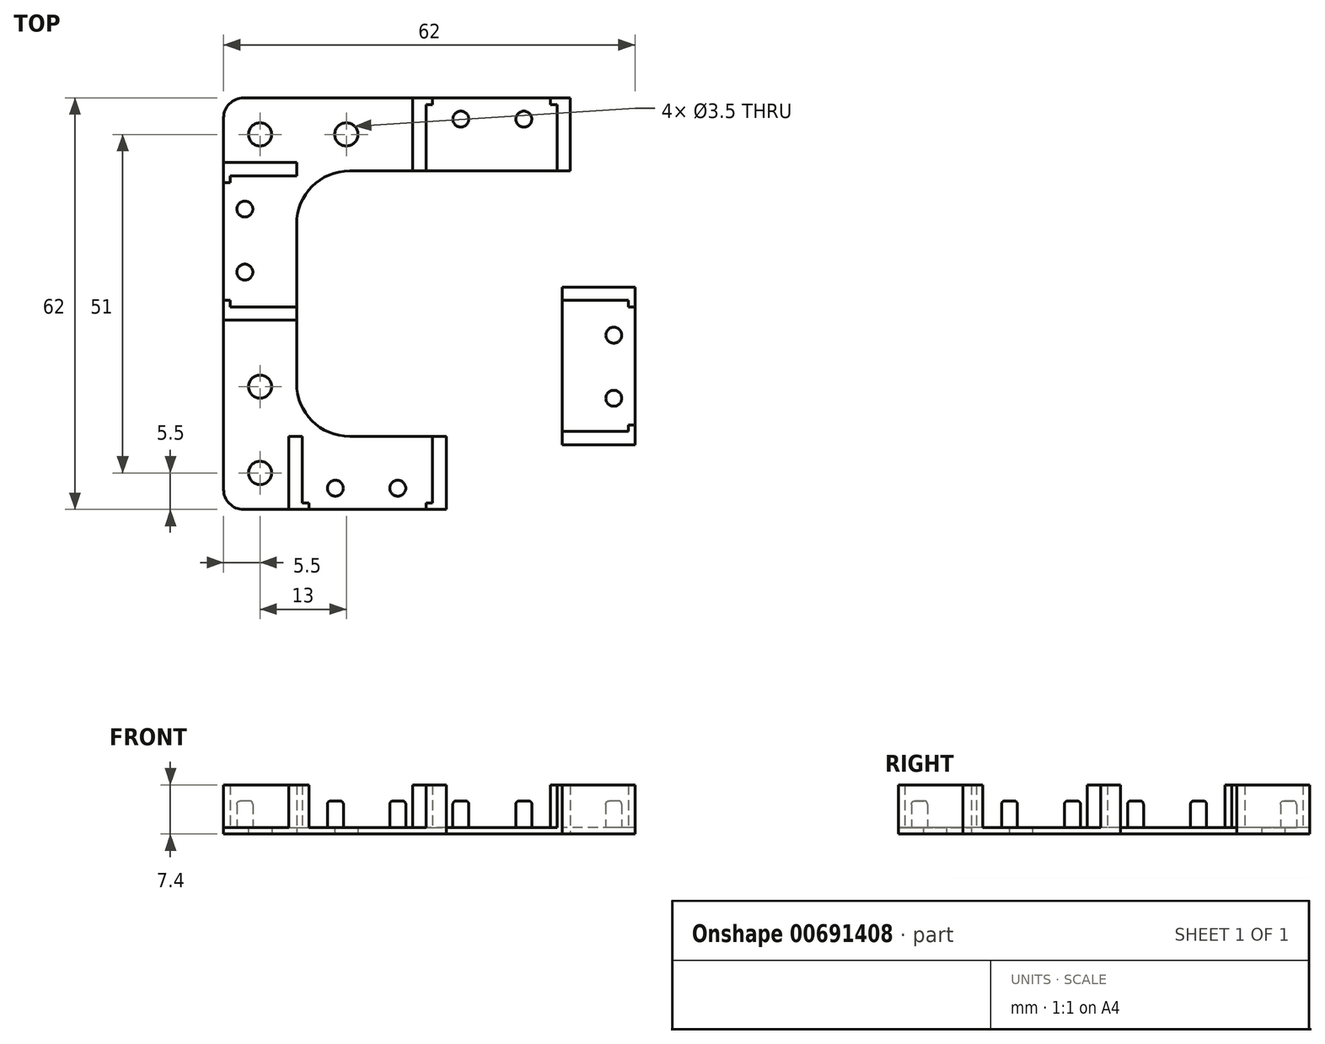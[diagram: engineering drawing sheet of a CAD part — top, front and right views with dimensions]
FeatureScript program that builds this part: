
annotation { "Feature Type Name" : "Feature", "Feature Type Description" : "" }
export const myFeature = defineFeature(function(context is Context, id is Id, definition is map)
    precondition{}
    {
        {
            var Q0;
            Q0=qCreatedBy(makeId("Top.planeOp"),FACE);
            var sketch = newSketch(context, id + "F0", { "sketchPlane" : qUnion([Q0])});
            skLineSegment(sketch, "E0.bottom", {"start": v(0, 20) * mm, "end": v(20, 20) * mm});
            skLineSegment(sketch, "E0.top", {"start": v(0, -20) * mm, "end": v(20, -20) * mm});
            skLineSegment(sketch, "E0.right", {"start": v(20, 20) * mm, "end": v(20, -20) * mm});
            skPoint(sketch, "E1", {"position": v(0, 20) * mm});
            skPoint(sketch, "E2", {"position": v(0, -20) * mm});
            skPoint(sketch, "E3", {"position": v(20, 0) * mm});
            skLineSegment(sketch, "E4.bottom", {"start": v(0, 31) * mm, "end": v(31, 31) * mm});
            skLineSegment(sketch, "E4.top", {"start": v(0, -31) * mm, "end": v(31, -31) * mm});
            skLineSegment(sketch, "E4.right", {"start": v(31, 31) * mm, "end": v(31, -31) * mm});
            skPoint(sketch, "E5", {"position": v(0, 31) * mm});
            skPoint(sketch, "E6", {"position": v(31, 0) * mm});
            skLineSegment(sketch, "E7.bottom", {"start": v(20, 2.5) * mm, "end": v(31, 2.5) * mm});
            skLineSegment(sketch, "E7.top", {"start": v(20, -21.25) * mm, "end": v(31, -21.25) * mm});
            skLineSegment(sketch, "E7.left", {"start": v(20, 2.5) * mm, "end": v(20, -21.25) * mm});
            skLineSegment(sketch, "E7.right", {"start": v(31, 2.5) * mm, "end": v(31, -21.25) * mm});
            skLineSegment(sketch, "E8", {"start": v(31, -0.5) * mm, "end": v(30, -0.5) * mm});
            skLineSegment(sketch, "E9", {"start": v(30, -0.5) * mm, "end": v(30, 0.5) * mm});
            skLineSegment(sketch, "E10", {"start": v(30, 0.5) * mm, "end": v(20, 0.5) * mm});
            skLineSegment(sketch, "E11", {"start": v(31, -18.25) * mm, "end": v(30, -18.25) * mm});
            skLineSegment(sketch, "E12", {"start": v(30, -18.25) * mm, "end": v(30, -19.25) * mm});
            skLineSegment(sketch, "E13", {"start": v(30, -19.25) * mm, "end": v(20, -19.25) * mm});
            skCircle(sketch, "E14", {"center": v(27.8, -14.25) * mm, "radius": 1.2 * mm});
            skCircle(sketch, "E15", {"center": v(27.8, -4.75) * mm, "radius": 1.2 * mm});
            skLineSegment(sketch, "E16", {"start": v(27.8, -4.75) * mm, "end": v(27.8, 0.5) * mm, "construction": true});
            skPoint(sketch, "E17", {"position": v(0, -31) * mm});
            skLineSegment(sketch, "E18.bottom", {"start": v(-17.16, -20) * mm, "end": v(2.6, -20) * mm});
            skLineSegment(sketch, "E18.top", {"start": v(-17.16, -31) * mm, "end": v(-3.68, -31) * mm});
            skLineSegment(sketch, "E18.left", {"start": v(-21.15, -20) * mm, "end": v(-21.15, -31) * mm});
            skLineSegment(sketch, "E18.right", {"start": v(2.6, -20) * mm, "end": v(2.6, -31) * mm});
            skLineSegment(sketch, "E19", {"start": v(-18.15, -31) * mm, "end": v(-18.15, -30) * mm});
            skLineSegment(sketch, "E20", {"start": v(-19.15, -30) * mm, "end": v(-19.15, -20) * mm});
            skLineSegment(sketch, "E21", {"start": v(-0.5, -31) * mm, "end": v(-0.5, -30) * mm});
            skLineSegment(sketch, "E22", {"start": v(-0.5, -30) * mm, "end": v(0.5, -30) * mm});
            skLineSegment(sketch, "E23", {"start": v(0.5, -30) * mm, "end": v(0.5, -20) * mm});
            skCircle(sketch, "E24", {"center": v(-14.15, -27.8) * mm, "radius": 1.2 * mm});
            skCircle(sketch, "E25", {"center": v(-4.75, -27.8) * mm, "radius": 1.2 * mm});
            skLineSegment(sketch, "E26.MirrorCS", {"start": v(0, 31) * mm, "end": v(-31, 31) * mm});
            skLineSegment(sketch, "E27.MirrorCS", {"start": v(0, 20) * mm, "end": v(-20, 20) * mm});
            skLineSegment(sketch, "E28.MirrorCS", {"start": v(-31, 31) * mm, "end": v(-31, -31) * mm});
            skLineSegment(sketch, "E29.MirrorCS", {"start": v(0, -31) * mm, "end": v(-31, -31) * mm});
            skLineSegment(sketch, "E30", {"start": v(-20, 20) * mm, "end": v(-20, -20) * mm});
            skLineSegment(sketch, "E31", {"start": v(-20, -20) * mm, "end": v(0, -20) * mm});
            skLineSegment(sketch, "E32.bottom", {"start": v(-31, 21.25) * mm, "end": v(-20, 21.25) * mm});
            skLineSegment(sketch, "E32.top", {"start": v(-31, -2.5) * mm, "end": v(-20, -2.5) * mm});
            skLineSegment(sketch, "E32.left", {"start": v(-31, 21.25) * mm, "end": v(-31, -2.5) * mm});
            skLineSegment(sketch, "E32.right", {"start": v(-20, 21.25) * mm, "end": v(-20, -2.5) * mm});
            skLineSegment(sketch, "E33", {"start": v(-31, 18.25) * mm, "end": v(-30, 18.25) * mm});
            skLineSegment(sketch, "E34", {"start": v(-30, 18.25) * mm, "end": v(-30, 19.25) * mm});
            skLineSegment(sketch, "E35", {"start": v(-30, 19.25) * mm, "end": v(-20, 19.25) * mm});
            skLineSegment(sketch, "E36", {"start": v(-31, 0.5) * mm, "end": v(-30, 0.5) * mm});
            skLineSegment(sketch, "E37", {"start": v(-30, 0.5) * mm, "end": v(-30, -0.5) * mm});
            skLineSegment(sketch, "E38", {"start": v(-30, -0.5) * mm, "end": v(-20, -0.5) * mm});
            skCircle(sketch, "E39", {"center": v(-27.8, 14.25) * mm, "radius": 1.2 * mm});
            skCircle(sketch, "E40", {"center": v(-27.8, 4.75) * mm, "radius": 1.2 * mm});
            skPoint(sketch, "E41.startSnap0", {"position": v(-31, 0) * mm});
            skLineSegment(sketch, "E42", {"start": v(-19.15, -30) * mm, "end": v(-18.15, -30) * mm});
            skLineSegment(sketch, "E43", {"start": v(-21.15, -20) * mm, "end": v(-20, -20) * mm});
            skLineSegment(sketch, "E44.bottom", {"start": v(-2.5, 31) * mm, "end": v(21.25, 31) * mm});
            skLineSegment(sketch, "E44.top", {"start": v(-2.5, 20) * mm, "end": v(21.25, 20) * mm});
            skLineSegment(sketch, "E44.left", {"start": v(-2.5, 31) * mm, "end": v(-2.5, 20) * mm});
            skLineSegment(sketch, "E44.right", {"start": v(21.25, 31) * mm, "end": v(21.25, 20) * mm});
            skLineSegment(sketch, "E45", {"start": v(0.5, 31) * mm, "end": v(0.5, 30) * mm});
            skLineSegment(sketch, "E46", {"start": v(0.5, 30) * mm, "end": v(-0.5, 30) * mm});
            skLineSegment(sketch, "E47", {"start": v(-0.5, 30) * mm, "end": v(-0.5, 20) * mm});
            skLineSegment(sketch, "E48", {"start": v(18.25, 31) * mm, "end": v(18.25, 30) * mm});
            skLineSegment(sketch, "E49", {"start": v(18.25, 30) * mm, "end": v(19.25, 30) * mm});
            skLineSegment(sketch, "E50", {"start": v(19.25, 30) * mm, "end": v(19.25, 20) * mm});
            skCircle(sketch, "E51", {"center": v(4.75, 27.8) * mm, "radius": 1.2 * mm});
            skCircle(sketch, "E52", {"center": v(14.25, 27.8) * mm, "radius": 1.2 * mm});
            skCircle(sketch, "E53", {"center": v(25.5, 25.5) * mm, "radius": 1.75 * mm});
            skCircle(sketch, "E54", {"center": v(-25.5, 25.5) * mm, "radius": 1.75 * mm});
            skCircle(sketch, "E55", {"center": v(-25.5, -25.5) * mm, "radius": 1.75 * mm});
            skCircle(sketch, "E56", {"center": v(25.5, -25.5) * mm, "radius": 1.75 * mm});
            skCircle(sketch, "E57", {"center": v(12.6, -25.5) * mm, "radius": 1.75 * mm});
            skPoint(sketch, "E57.centerSnap0", {"position": v(2.6, -25.5) * mm});
            skCircle(sketch, "E58", {"center": v(-25.5, -12.5) * mm, "radius": 1.75 * mm});
            skCircle(sketch, "E59", {"center": v(-12.5, 25.5) * mm, "radius": 1.75 * mm});
            skCircle(sketch, "E60", {"center": v(25.5, 12.5) * mm, "radius": 1.75 * mm});
            skSolve(sketch);
        }
        {
            var Q0;
            {var subQ1=sQuery(id+"F0.wireOp",EDGE,"E44.left");Q0=makeQuery(id+"F0.imprint","IMPRINT",FACE,{"disambiguationData":[TD([[makeQuery(id+"F0.imprint","IMPRINT",EDGE,{"derivedFrom":subQ1}),1.0]])]});}
            var Q1;
            {var subQ0=sQuery(id+"F0.wireOp",EDGE,"E44.right");Q1=makeQuery(id+"F0.imprint","IMPRINT",FACE,{"disambiguationData":[TD([[makeQuery(id+"F0.imprint","IMPRINT",EDGE,{"derivedFrom":subQ0}),-1.0]])]});}
            var Q2;
            {var subQ2=sQuery(id+"F0.wireOp",EDGE,"E7.bottom");Q2=makeQuery(id+"F0.imprint","IMPRINT",FACE,{"disambiguationData":[TD([[makeQuery(id+"F0.imprint","IMPRINT",EDGE,{"derivedFrom":subQ2}),-1.0]])]});}
            var Q3;
            {var subQ1=sQuery(id+"F0.wireOp",EDGE,"E7.top");Q3=makeQuery(id+"F0.imprint","IMPRINT",FACE,{"disambiguationData":[TD([[makeQuery(id+"F0.imprint","IMPRINT",EDGE,{"derivedFrom":subQ1}),1.0]])]});}
            var Q4;
            {var subQ0=sQuery(id+"F0.wireOp",EDGE,"E18.right");Q4=makeQuery(id+"F0.imprint","IMPRINT",FACE,{"disambiguationData":[TD([[makeQuery(id+"F0.imprint","IMPRINT",EDGE,{"derivedFrom":subQ0}),-1.0]])]});}
            var Q5;
            {var subQ3=sQuery(id+"F0.wireOp",EDGE,"E18.left");Q5=makeQuery(id+"F0.imprint","IMPRINT",FACE,{"disambiguationData":[TD([[makeQuery(id+"F0.imprint","IMPRINT",EDGE,{"derivedFrom":subQ3}),1.0]])]});}
            var Q6;
            {var subQ1=sQuery(id+"F0.wireOp",EDGE,"E32.top");Q6=makeQuery(id+"F0.imprint","IMPRINT",FACE,{"disambiguationData":[TD([[makeQuery(id+"F0.imprint","IMPRINT",EDGE,{"derivedFrom":subQ1}),1.0]])]});}
            var Q7;
            {var subQ4=sQuery(id+"F0.wireOp",EDGE,"E32.bottom");Q7=makeQuery(id+"F0.imprint","IMPRINT",FACE,{"disambiguationData":[TD([[makeQuery(id+"F0.imprint","IMPRINT",EDGE,{"derivedFrom":subQ4}),-1.0]])]});}
            extrude(context, id + "F1", {"entities" : qUnion([Q0, Q1, Q2, Q3, Q4, Q5, Q6, Q7]), "depth" : 7.4 * mm, "offsetDistance" : 25 * mm});
        }
        {
            var Q0;
            Q0=makeQuery(id+"F0.imprint","IMPRINT",FACE,{"disambiguationData":[TD([[makeQuery(id+"F0.imprint","IMPRINT",EDGE,{"derivedFrom":sQuery(id+"F0.wireOp",EDGE,"E51")}),1.0]])]});
            var Q1;
            Q1=makeQuery(id+"F0.imprint","IMPRINT",FACE,{"disambiguationData":[TD([[makeQuery(id+"F0.imprint","IMPRINT",EDGE,{"derivedFrom":sQuery(id+"F0.wireOp",EDGE,"E52")}),1.0]])]});
            var Q2;
            Q2=makeQuery(id+"F0.imprint","IMPRINT",FACE,{"disambiguationData":[TD([[makeQuery(id+"F0.imprint","IMPRINT",EDGE,{"derivedFrom":sQuery(id+"F0.wireOp",EDGE,"E15")}),1.0]])]});
            var Q3;
            Q3=makeQuery(id+"F0.imprint","IMPRINT",FACE,{"disambiguationData":[TD([[makeQuery(id+"F0.imprint","IMPRINT",EDGE,{"derivedFrom":sQuery(id+"F0.wireOp",EDGE,"E14")}),1.0]])]});
            var Q4;
            Q4=makeQuery(id+"F0.imprint","IMPRINT",FACE,{"disambiguationData":[TD([[makeQuery(id+"F0.imprint","IMPRINT",EDGE,{"derivedFrom":sQuery(id+"F0.wireOp",EDGE,"E25")}),1.0]])]});
            var Q5;
            Q5=makeQuery(id+"F0.imprint","IMPRINT",FACE,{"disambiguationData":[TD([[makeQuery(id+"F0.imprint","IMPRINT",EDGE,{"derivedFrom":sQuery(id+"F0.wireOp",EDGE,"E24")}),1.0]])]});
            var Q6;
            Q6=makeQuery(id+"F0.imprint","IMPRINT",FACE,{"disambiguationData":[TD([[makeQuery(id+"F0.imprint","IMPRINT",EDGE,{"derivedFrom":sQuery(id+"F0.wireOp",EDGE,"E39")}),1.0]])]});
            var Q7;
            Q7=makeQuery(id+"F0.imprint","IMPRINT",FACE,{"disambiguationData":[TD([[makeQuery(id+"F0.imprint","IMPRINT",EDGE,{"derivedFrom":sQuery(id+"F0.wireOp",EDGE,"E40")}),1.0]])]});
            extrude(context, id + "F2", {"entities" : qUnion([Q0, Q1, Q2, Q3, Q4, Q5, Q6, Q7]), "operationType" : NewBodyOperationType.ADD, "depth" : 5 * mm, "offsetDistance" : 25 * mm});
        }
        {
            var Q0;
            {var subQ0=sQuery(id+"F0.wireOp",EDGE,"E45");Q0=makeQuery(id+"F0.imprint","IMPRINT",FACE,{"disambiguationData":[TD([[makeQuery(id+"F0.imprint","IMPRINT",EDGE,{"derivedFrom":subQ0}),1.0]])]});}
            var Q1;
            {var subQ3=sQuery(id+"F0.wireOp",EDGE,"E26.MirrorCS");Q1=makeQuery(id+"F0.imprint","IMPRINT",FACE,{"disambiguationData":[TD([[makeQuery(id+"F0.imprint","IMPRINT",EDGE,{"derivedFrom":subQ3}),1.0]])]});}
            var Q2;
            {var subQ0=sQuery(id+"F0.wireOp",EDGE,"E33");Q2=makeQuery(id+"F0.imprint","IMPRINT",FACE,{"disambiguationData":[TD([[makeQuery(id+"F0.imprint","IMPRINT",EDGE,{"derivedFrom":subQ0}),-1.0]])]});}
            var Q3;
            {var subQ1=sQuery(id+"F0.wireOp",EDGE,"E18.left");Q3=makeQuery(id+"F0.imprint","IMPRINT",FACE,{"disambiguationData":[TD([[makeQuery(id+"F0.imprint","IMPRINT",EDGE,{"derivedFrom":subQ1}),-1.0]])]});}
            var Q4;
            {var subQ7=sQuery(id+"F0.wireOp",EDGE,"E19");Q4=makeQuery(id+"F0.imprint","IMPRINT",FACE,{"disambiguationData":[TD([[makeQuery(id+"F0.imprint","IMPRINT",EDGE,{"derivedFrom":subQ7}),-1.0]])]});}
            var Q5;
            {var subQ5=sQuery(id+"F0.wireOp",EDGE,"E0.top");Q5=makeQuery(id+"F0.imprint","IMPRINT",FACE,{"disambiguationData":[TD([[makeQuery(id+"F0.imprint","IMPRINT",EDGE,{"derivedFrom":subQ5}),-1.0]])]});}
            var Q6;
            {var subQ0=sQuery(id+"F0.wireOp",EDGE,"E8");Q6=makeQuery(id+"F0.imprint","IMPRINT",FACE,{"disambiguationData":[TD([[makeQuery(id+"F0.imprint","IMPRINT",EDGE,{"derivedFrom":subQ0}),1.0]])]});}
            var Q7;
            {var subQ3=sQuery(id+"F0.wireOp",EDGE,"E0.right");Q7=makeQuery(id+"F0.imprint","IMPRINT",FACE,{"disambiguationData":[TD([[makeQuery(id+"F0.imprint","IMPRINT",EDGE,{"derivedFrom":subQ3}),1.0]])]});}
            extrude(context, id + "F3", {"entities" : qUnion([Q0, Q1, Q2, Q3, Q4, Q5, Q6, Q7]), "operationType" : NewBodyOperationType.ADD, "depth" : 1 * mm, "offsetDistance" : 25 * mm});
        }
        {
            var Q0;
            Q0=makeQuery(id+"F3.opExtrude","SWEPT_EDGE",EDGE,{"disambiguationData":[OSD([sQuery(id+"F0.wireOp",EDGE,"E26.MirrorCS"),sQuery(id+"F0.wireOp",EDGE,"E28.MirrorCS")])]});
            var Q1;
            Q1=makeQuery(id+"F3.opExtrude","SWEPT_EDGE",EDGE,{"disambiguationData":[OSD([sQuery(id+"F0.wireOp",EDGE,"E4.bottom"),sQuery(id+"F0.wireOp",EDGE,"E4.right")])]});
            var Q2;
            Q2=makeQuery(id+"F3.opExtrude","SWEPT_EDGE",EDGE,{"disambiguationData":[OSD([sQuery(id+"F0.wireOp",EDGE,"E4.top"),sQuery(id+"F0.wireOp",EDGE,"E4.right")])]});
            var Q3;
            Q3=makeQuery(id+"F3.opExtrude","SWEPT_EDGE",EDGE,{"disambiguationData":[OSD([sQuery(id+"F0.wireOp",EDGE,"E28.MirrorCS"),sQuery(id+"F0.wireOp",EDGE,"E29.MirrorCS")])]});
            fillet(context, id + "F4", {"entities" : qUnion([Q0, Q1, Q2, Q3]), "radius" : 3 * mm, "tangentPropagation" : true, "allowEdgeOverflow" : false});
        }
        {
            var Q0;
            Q0=makeQuery(id+"F2.opExtrude","CAP_EDGE",EDGE,{"disambiguationData":[OSD([sQuery(id+"F0.wireOp",EDGE,"E52")])],"isStart":false});
            var Q1;
            Q1=makeQuery(id+"F2.opExtrude","CAP_EDGE",EDGE,{"disambiguationData":[OSD([sQuery(id+"F0.wireOp",EDGE,"E51")])],"isStart":false});
            var Q2;
            Q2=makeQuery(id+"F2.opExtrude","CAP_EDGE",EDGE,{"disambiguationData":[OSD([sQuery(id+"F0.wireOp",EDGE,"E39")])],"isStart":false});
            var Q3;
            Q3=makeQuery(id+"F2.opExtrude","CAP_EDGE",EDGE,{"disambiguationData":[OSD([sQuery(id+"F0.wireOp",EDGE,"E40")])],"isStart":false});
            var Q4;
            Q4=makeQuery(id+"F2.opExtrude","CAP_EDGE",EDGE,{"disambiguationData":[OSD([sQuery(id+"F0.wireOp",EDGE,"E15")])],"isStart":false});
            var Q5;
            Q5=makeQuery(id+"F2.opExtrude","CAP_EDGE",EDGE,{"disambiguationData":[OSD([sQuery(id+"F0.wireOp",EDGE,"E14")])],"isStart":false});
            var Q6;
            Q6=makeQuery(id+"F2.opExtrude","CAP_EDGE",EDGE,{"disambiguationData":[OSD([sQuery(id+"F0.wireOp",EDGE,"E25")])],"isStart":false});
            var Q7;
            Q7=makeQuery(id+"F2.opExtrude","CAP_EDGE",EDGE,{"disambiguationData":[OSD([sQuery(id+"F0.wireOp",EDGE,"E24")])],"isStart":false});
            fillet(context, id + "F5", {"entities" : qUnion([Q0, Q1, Q2, Q3, Q4, Q5, Q6, Q7]), "radius" : 0.5 * mm, "tangentPropagation" : true, "allowEdgeOverflow" : false});
        }
        {
            var Q0;
            Q0=makeQuery(id+"F3.opExtrude","SWEPT_EDGE",EDGE,{"disambiguationData":[OSD([sQuery(id+"F0.wireOp",EDGE,"E30"),sQuery(id+"F0.wireOp",EDGE,"E31"),sQuery(id+"F0.wireOp",EDGE,"E43")])]});
            var Q1;
            Q1=makeQuery(id+"F3.opExtrude","SWEPT_EDGE",EDGE,{"disambiguationData":[OSD([sQuery(id+"F0.wireOp",EDGE,"E0.top"),sQuery(id+"F0.wireOp",EDGE,"E7.left")])]});
            var Q2;
            Q2=makeQuery(id+"F3.opExtrude","SWEPT_EDGE",EDGE,{"disambiguationData":[OSD([sQuery(id+"F0.wireOp",EDGE,"E0.right"),sQuery(id+"F0.wireOp",EDGE,"E44.top")])]});
            var Q3;
            Q3=makeQuery(id+"F3.opExtrude","SWEPT_EDGE",EDGE,{"disambiguationData":[OSD([sQuery(id+"F0.wireOp",EDGE,"E27.MirrorCS"),sQuery(id+"F0.wireOp",EDGE,"E32.right")])]});
            fillet(context, id + "F6", {"entities" : qUnion([Q0, Q1, Q2, Q3]), "radius" : 8 * mm, "tangentPropagation" : true, "allowEdgeOverflow" : false});
        }
    });
